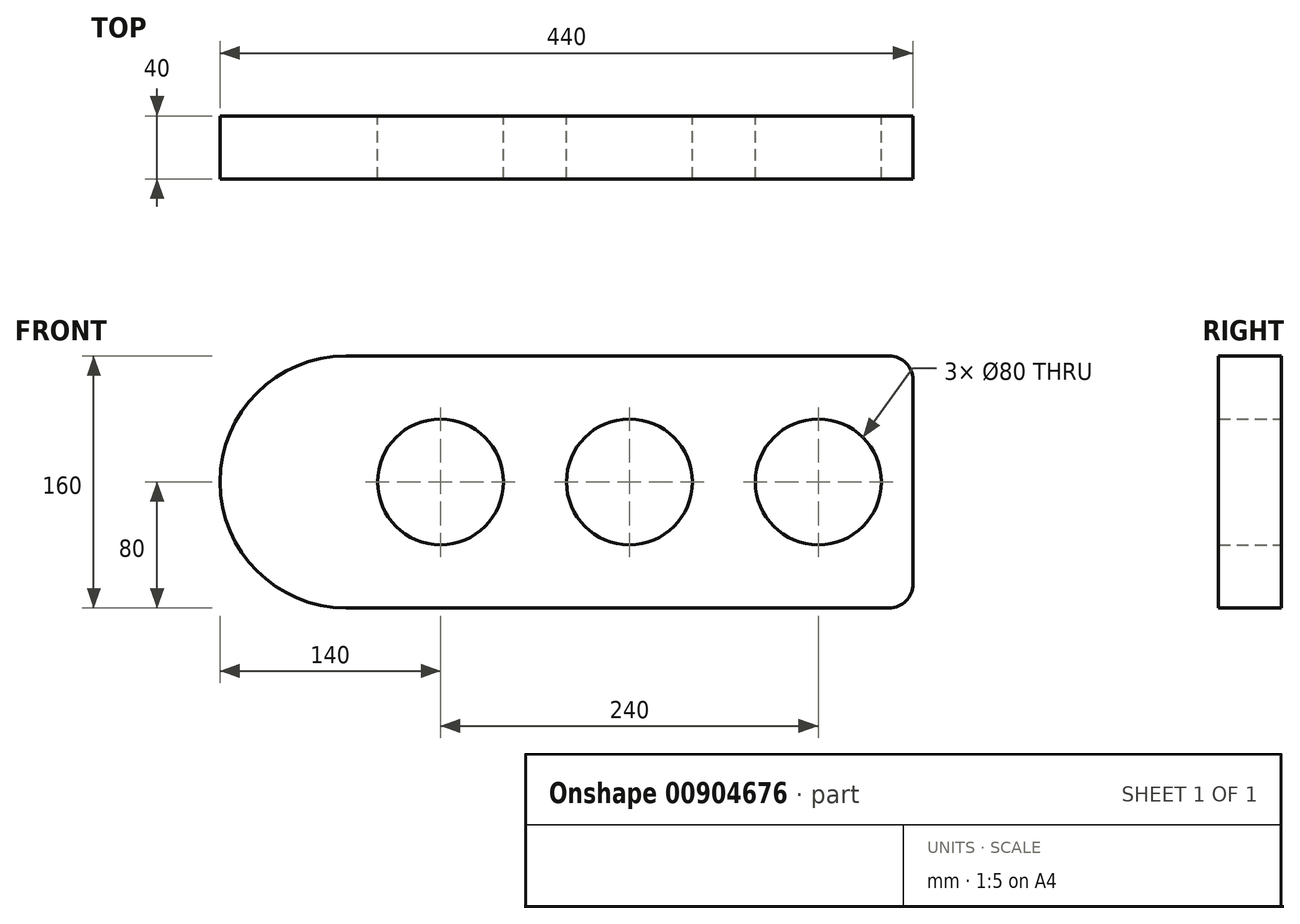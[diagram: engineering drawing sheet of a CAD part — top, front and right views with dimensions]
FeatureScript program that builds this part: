
annotation { "Feature Type Name" : "Feature", "Feature Type Description" : "" }
export const myFeature = defineFeature(function(context is Context, id is Id, definition is map)
    precondition{}
    {
        {
            var Q0;
            Q0=qCreatedBy(makeId("Front.planeOp"),FACE);
            var sketch = newSketch(context, id + "F0", { "sketchPlane" : qUnion([Q0])});
            skCircle(sketch, "E0", {"center": v(0, 0) * mm, "radius": 40 * mm});
            skCircle(sketch, "E1", {"center": v(-120, 0) * mm, "radius": 40 * mm});
            skCircle(sketch, "E2", {"center": v(120, 0) * mm, "radius": 40 * mm});
            skLineSegment(sketch, "E3", {"start": v(-20, -80) * mm, "end": v(-180, -80) * mm});
            skLineSegment(sketch, "E4", {"start": v(0, 80) * mm, "end": v(120, 80) * mm});
            skLineSegment(sketch, "E5", {"start": v(120, 80) * mm, "end": v(0, 80) * mm});
            skLineSegment(sketch, "E6", {"start": v(0, 80) * mm, "end": v(-180, 80) * mm});
            skArc(sketch, "E7", {"start": v(-180, 80) * mm, "mid": v(-260, 0) * mm, "end": v(-180, -80) * mm});
            skPoint(sketch, "E8.center.orphan", {"position": v(180, -11.25) * mm});
            skPoint(sketch, "E9.end.orphan", {"position": v(180, -80) * mm});
            skLineSegment(sketch, "E10", {"start": v(-20, -80) * mm, "end": v(180, -80) * mm});
            skLineSegment(sketch, "E11", {"start": v(120, 80) * mm, "end": v(180, 80) * mm});
            skLineSegment(sketch, "E12", {"start": v(180, 80) * mm, "end": v(180, -80) * mm});
            skSolve(sketch);
        }
        {
            var Q0;
            Q0 = qSketchRegion(id + "F0", true);
            extrude(context, id + "F1", {"entities" : qUnion([Q0]), "depth" : 40 * mm, "offsetDistance" : 25 * mm});
        }
        {
            var Q0;
            Q0=makeQuery(id+"F1.opExtrude","SWEPT_EDGE",EDGE,{"disambiguationData":[OSD([sQuery(id+"F0.wireOp",EDGE,"E11"),sQuery(id+"F0.wireOp",EDGE,"E12")])]});
            var Q1;
            Q1=makeQuery(id+"F1.opExtrude","SWEPT_EDGE",EDGE,{"disambiguationData":[OSD([sQuery(id+"F0.wireOp",EDGE,"E10"),sQuery(id+"F0.wireOp",EDGE,"E12")])]});
            fillet(context, id + "F2", {"entities" : qUnion([Q0, Q1]), "radius" : 15 * mm, "tangentPropagation" : true, "allowEdgeOverflow" : false});
        }
    });
